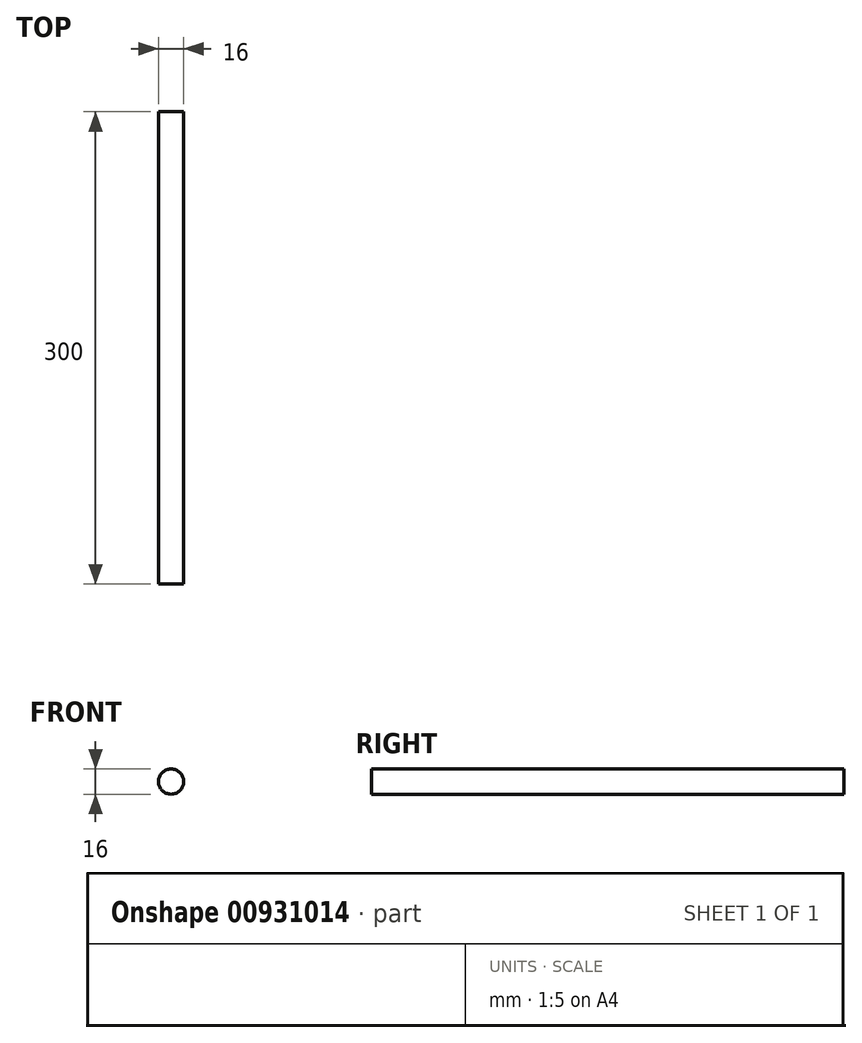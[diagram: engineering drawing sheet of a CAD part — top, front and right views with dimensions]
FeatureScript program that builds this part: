
annotation { "Feature Type Name" : "Feature", "Feature Type Description" : "" }
export const myFeature = defineFeature(function(context is Context, id is Id, definition is map)
    precondition{}
    {
        {
            var Q0;
            Q0=qCreatedBy(makeId("Front.planeOp"),FACE);
            var sketch = newSketch(context, id + "F0", { "sketchPlane" : qUnion([Q0])});
            skCircle(sketch, "E0", {"center": v(0, 0) * mm, "radius": 8 * mm});
            skSolve(sketch);
        }
        {
            var Q0;
            Q0 = qSketchRegion(id + "F0", true);
            extrude(context, id + "F1", {"entities" : qUnion([Q0]), "oppositeDirection" : true, "depth" : 300 * mm, "offsetDistance" : 25 * mm});
        }
    });
